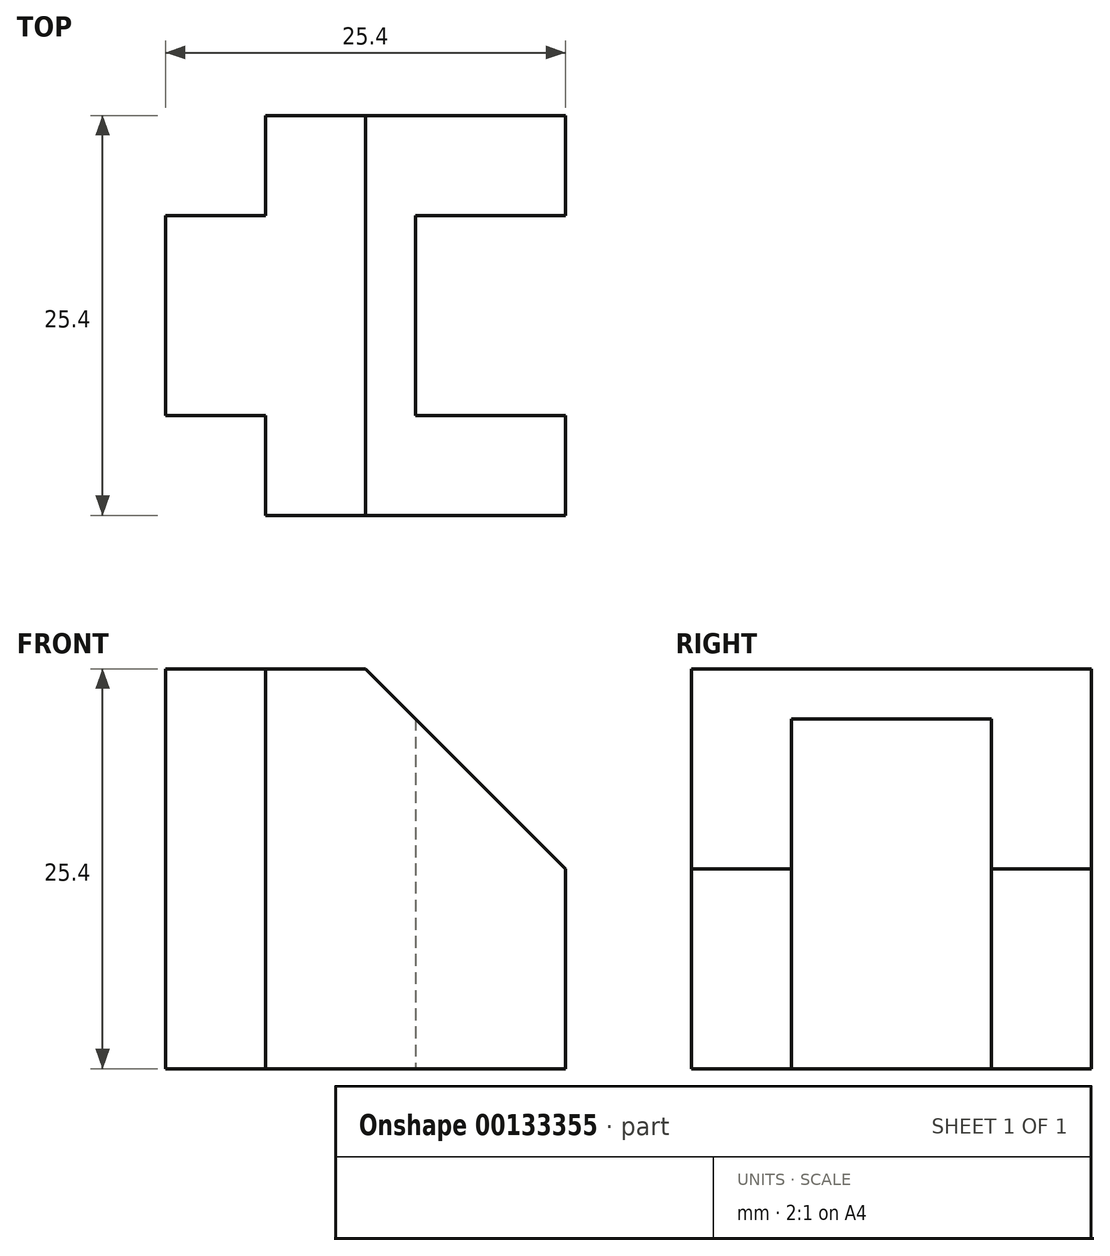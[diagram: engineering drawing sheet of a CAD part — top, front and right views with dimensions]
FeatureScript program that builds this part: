
annotation { "Feature Type Name" : "Feature", "Feature Type Description" : "" }
export const myFeature = defineFeature(function(context is Context, id is Id, definition is map)
    precondition{}
    {
        {
            var Q0;
            Q0=qCreatedBy(makeId("Top.planeOp"),FACE);
            var sketch = newSketch(context, id + "F0", { "sketchPlane" : qUnion([Q0])});
            skLineSegment(sketch, "E0", {"start": v(0, 0) * mm, "end": v(6.35, 0) * mm});
            skLineSegment(sketch, "E1", {"start": v(6.35, 0) * mm, "end": v(6.35, 25.4) * mm});
            skLineSegment(sketch, "E2", {"start": v(6.35, 25.4) * mm, "end": v(0, 25.4) * mm});
            skLineSegment(sketch, "E3", {"start": v(0, 25.4) * mm, "end": v(0, 19.05) * mm});
            skLineSegment(sketch, "E4", {"start": v(0, 19.05) * mm, "end": v(-6.35, 19.05) * mm});
            skLineSegment(sketch, "E5", {"start": v(-6.35, 19.05) * mm, "end": v(-6.35, 6.35) * mm});
            skLineSegment(sketch, "E6", {"start": v(-6.35, 6.35) * mm, "end": v(0, 6.35) * mm});
            skLineSegment(sketch, "E7", {"start": v(0, 6.35) * mm, "end": v(0, 0) * mm});
            skLineSegment(sketch, "E8", {"start": v(6.35, 25.4) * mm, "end": v(19.05, 25.4) * mm});
            skLineSegment(sketch, "E9", {"start": v(19.05, 25.4) * mm, "end": v(19.05, 19.05) * mm});
            skLineSegment(sketch, "E10", {"start": v(19.05, 19.05) * mm, "end": v(9.53, 19.05) * mm});
            skLineSegment(sketch, "E11", {"start": v(9.53, 19.05) * mm, "end": v(9.53, 6.35) * mm});
            skLineSegment(sketch, "E12", {"start": v(9.52, 6.35) * mm, "end": v(19.05, 6.35) * mm});
            skLineSegment(sketch, "E13", {"start": v(19.05, 6.35) * mm, "end": v(19.05, 0) * mm});
            skLineSegment(sketch, "E14", {"start": v(19.05, 0) * mm, "end": v(6.35, 0) * mm});
            skSolve(sketch);
        }
        {
            var Q0;
            Q0=makeQuery(id+"F0.imprint","IMPRINT",FACE,{"disambiguationData":[TD([[makeQuery(id+"F0.imprint","IMPRINT",EDGE,{"derivedFrom":sQuery(id+"F0.wireOp",EDGE,"E0")}),1.0]])]});
            var Q1;
            Q1=makeQuery(id+"F0.imprint","IMPRINT",FACE,{"disambiguationData":[TD([[makeQuery(id+"F0.imprint","IMPRINT",EDGE,{"derivedFrom":sQuery(id+"F0.wireOp",EDGE,"E1")}),-1.0]])]});
            extrude(context, id + "F1", {"entities" : qUnion([Q0, Q1]), "depth" : 25.4 * mm});
        }
        {
            var Q0;
            Q0=makeQuery(id+"F1.opExtrude","SWEPT_FACE",FACE,{"disambiguationData":[OSD([sQuery(id+"F0.wireOp",EDGE,"E0"),sQuery(id+"F0.wireOp",EDGE,"E14")])]});
            var sketch = newSketch(context, id + "F2", { "sketchPlane" : qUnion([Q0])});
            skLineSegment(sketch, "E15.bottom", {"start": v(0, 25.4) * mm, "end": v(19.05, 25.4) * mm});
            skLineSegment(sketch, "E15.top", {"start": v(0, 0) * mm, "end": v(19.05, 0) * mm});
            skLineSegment(sketch, "E15.left", {"start": v(0, 25.4) * mm, "end": v(0, 0) * mm});
            skLineSegment(sketch, "E15.right", {"start": v(19.05, 25.4) * mm, "end": v(19.05, 0) * mm});
            skLineSegment(sketch, "E16", {"start": v(6.35, 25.4) * mm, "end": v(19.05, 12.7) * mm});
            skSolve(sketch);
        }
        {
            var Q0;
            {var subQ3=sQuery(id+"F2.wireOp",EDGE,"E16");Q0=makeQuery(id+"F2.imprint","IMPRINT",FACE,{"disambiguationData":[TD([[makeQuery(id+"F2.imprint","IMPRINT",EDGE,{"derivedFrom":subQ3}),1.0]])]});}
            extrude(context, id + "F3", {"entities" : qUnion([Q0]), "operationType" : NewBodyOperationType.REMOVE, "oppositeDirection" : true, "depth" : 25.4 * mm});
        }
    });
